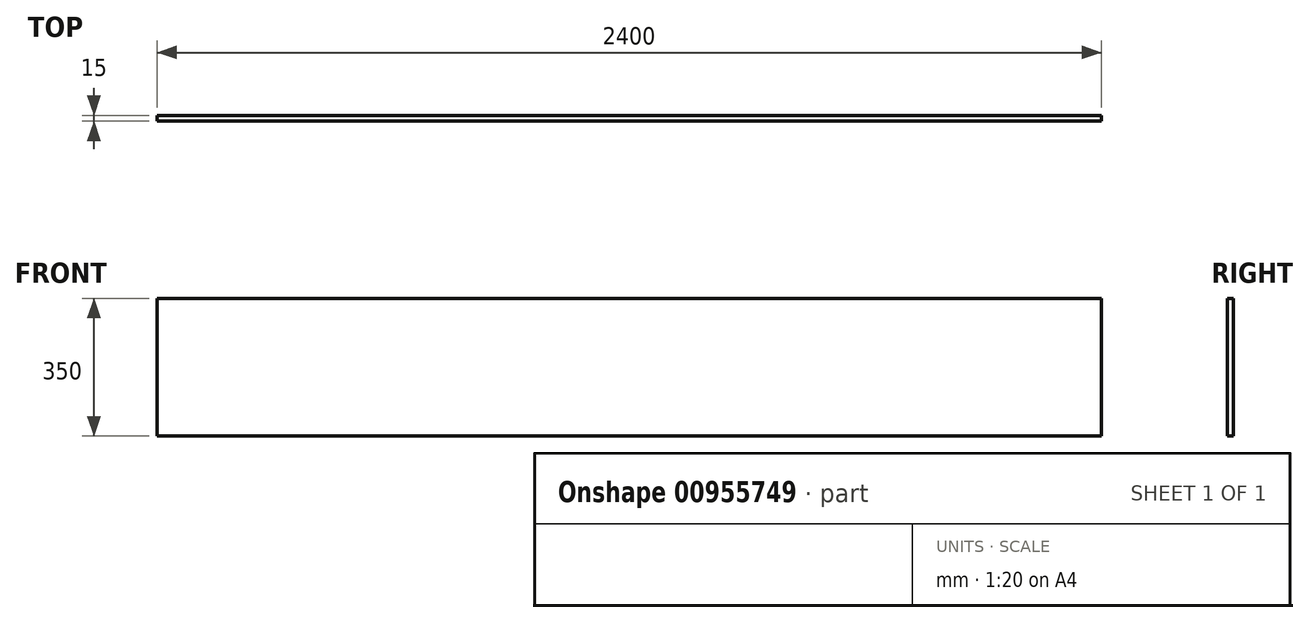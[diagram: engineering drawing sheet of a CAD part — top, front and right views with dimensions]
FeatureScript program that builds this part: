
annotation { "Feature Type Name" : "Feature", "Feature Type Description" : "" }
export const myFeature = defineFeature(function(context is Context, id is Id, definition is map)
    precondition{}
    {
        {
            var Q0;
            Q0=qCreatedBy(makeId("Front.planeOp"),FACE);
            var sketch = newSketch(context, id + "F0", { "sketchPlane" : qUnion([Q0])});
            skLineSegment(sketch, "E0.bottom", {"start": v(0, 0) * mm, "end": v(2400, 0) * mm});
            skLineSegment(sketch, "E0.top", {"start": v(0, -350) * mm, "end": v(2400, -350) * mm});
            skLineSegment(sketch, "E0.left", {"start": v(0, 0) * mm, "end": v(0, -350) * mm});
            skLineSegment(sketch, "E0.right", {"start": v(2400, 0) * mm, "end": v(2400, -350) * mm});
            skSolve(sketch);
        }
        {
            var Q0;
            Q0 = qSketchRegion(id + "F0", true);
            extrude(context, id + "F1", {"entities" : qUnion([Q0]), "depth" : 15 * mm, "offsetDistance" : 25 * mm});
        }
    });
